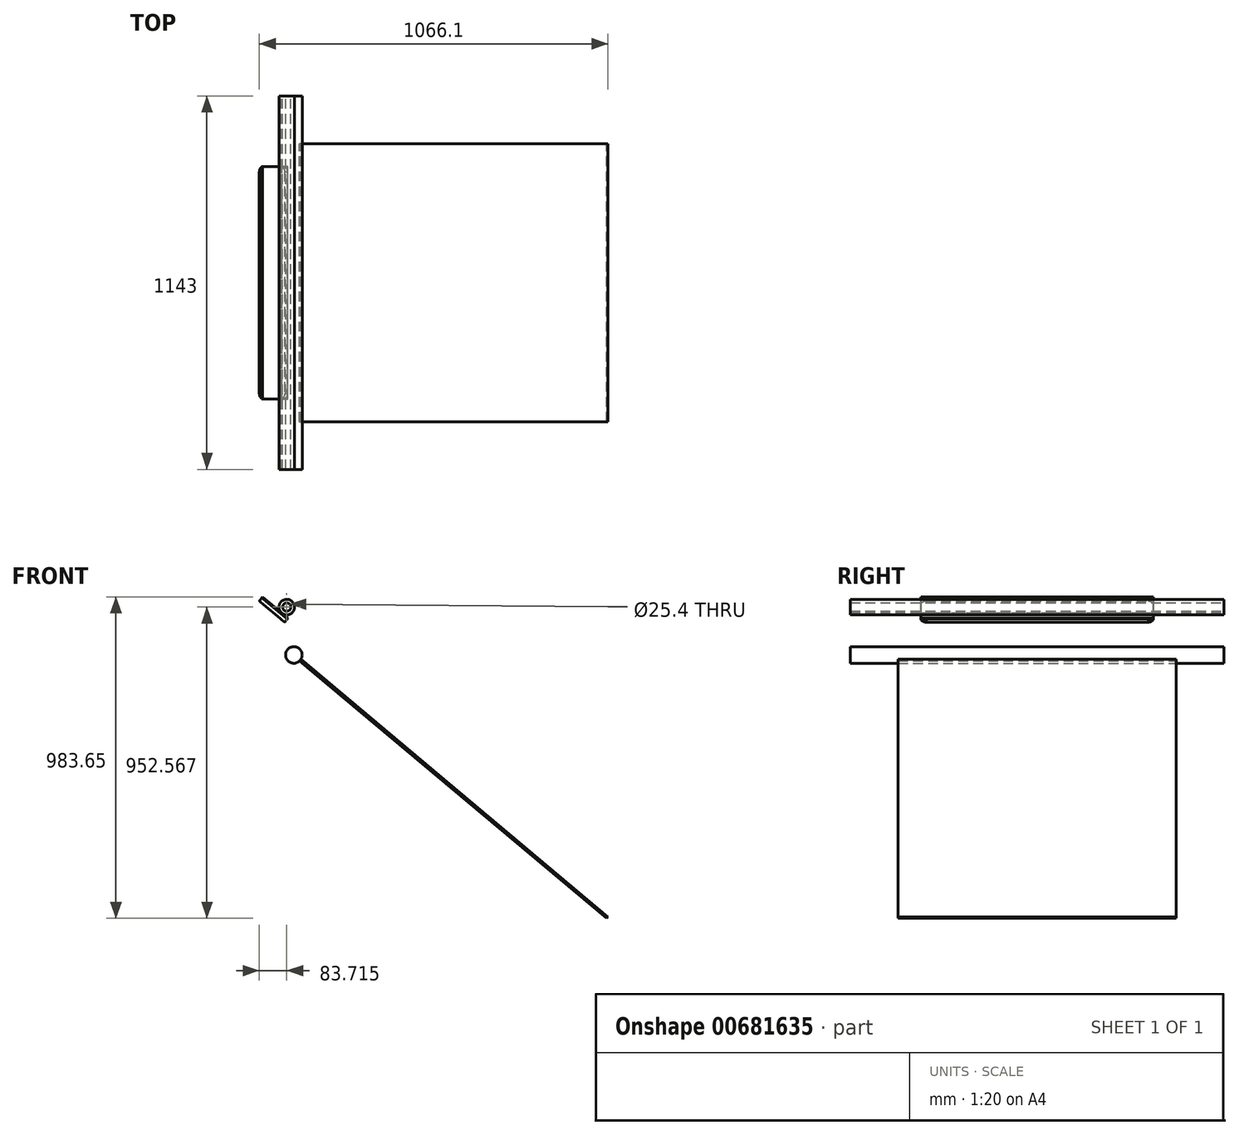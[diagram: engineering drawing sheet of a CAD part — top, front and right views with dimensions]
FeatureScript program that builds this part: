
annotation { "Feature Type Name" : "Feature", "Feature Type Description" : "" }
export const myFeature = defineFeature(function(context is Context, id is Id, definition is map)
    precondition{}
    {
        {
            var Q0;
            Q0=qCreatedBy(makeId("Front.planeOp"),FACE);
            var sketch = newSketch(context, id + "F0", { "sketchPlane" : qUnion([Q0])});
            skCircle(sketch, "E0", {"center": v(-203.72, 333.8) * mm, "radius": 23.81 * mm});
            skCircle(sketch, "E1", {"center": v(-203.72, 333.8) * mm, "radius": 12.7 * mm});
            skLineSegment(sketch, "E2", {"start": v(-179.5, 190.05) * mm, "end": v(778.67, -613.9) * mm});
            skLineSegment(sketch, "E3", {"start": v(778.67, -613.9) * mm, "end": v(774.59, -618.77) * mm});
            skLineSegment(sketch, "E4", {"start": v(774.59, -618.77) * mm, "end": v(-183.6, 185.2) * mm});
            skCircle(sketch, "E5", {"center": v(-181.85, 187.24) * mm, "radius": 25.4 * mm});
            skLineSegment(sketch, "E6", {"start": v(-179.5, 190.05) * mm, "end": v(-183.6, 185.2) * mm});
            skLineSegment(sketch, "E7", {"start": v(-219.42, 315.9) * mm, "end": v(-277.8, 364.88) * mm});
            skLineSegment(sketch, "E8", {"start": v(-277.8, 364.88) * mm, "end": v(-279.84, 362.45) * mm});
            skLineSegment(sketch, "E9", {"start": v(-279.84, 362.45) * mm, "end": v(-202, 297.14) * mm});
            skLineSegment(sketch, "E10", {"start": v(-202, 297.14) * mm, "end": v(-199.97, 299.57) * mm});
            skLineSegment(sketch, "E11", {"start": v(-199.97, 299.57) * mm, "end": v(-219.42, 315.9) * mm});
            skLineSegment(sketch, "E12", {"start": v(-219.42, 315.9) * mm, "end": v(-253.35, 382.47) * mm, "construction": true});
            skSolve(sketch);
        }
        {
            var Q0;
            {var subQ0=sQuery(id+"F0.wireOp",EDGE,"E3");Q0=makeQuery(id+"F0.imprint","IMPRINT",FACE,{"disambiguationData":[TD([[makeQuery(id+"F0.imprint","IMPRINT",EDGE,{"derivedFrom":subQ0}),-1.0]])]});}
            extrude(context, id + "F1", {"entities" : qUnion([Q0]), "endBound" : BoundingType.SYMMETRIC, "depth" : 850.9 * mm, "offsetDistance" : 25.4 * mm});
        }
        {
            var Q0;
            {var subQ0=sQuery(id+"F0.wireOp",EDGE,"E6");Q0=makeQuery(id+"F0.imprint","IMPRINT",FACE,{"disambiguationData":[TD([[makeQuery(id+"F0.imprint","IMPRINT",EDGE,{"derivedFrom":subQ0}),1.0]])]});}
            var Q1;
            {var subQ0=sQuery(id+"F0.wireOp",EDGE,"E6");Q1=makeQuery(id+"F0.imprint","IMPRINT",FACE,{"disambiguationData":[TD([[makeQuery(id+"F0.imprint","IMPRINT",EDGE,{"derivedFrom":subQ0}),-1.0]])]});}
            extrude(context, id + "F2", {"entities" : qUnion([Q0, Q1]), "operationType" : NewBodyOperationType.ADD, "endBound" : BoundingType.SYMMETRIC, "depth" : 1143 * mm, "offsetDistance" : 25.4 * mm});
        }
        {
            var Q0;
            Q0=makeQuery(id+"F0.imprint","IMPRINT",FACE,{"disambiguationData":[TD([[makeQuery(id+"F0.imprint","IMPRINT",EDGE,{"derivedFrom":sQuery(id+"F0.wireOp",EDGE,"E1")}),-1.0]])]});
            extrude(context, id + "F3", {"entities" : qUnion([Q0]), "endBound" : BoundingType.SYMMETRIC, "depth" : 1143 * mm, "offsetDistance" : 25.4 * mm});
        }
        {
            var Q0;
            {var subQ0=sQuery(id+"F0.wireOp",EDGE,"E7");Q0=makeQuery(id+"F0.imprint","IMPRINT",FACE,{"disambiguationData":[TD([[makeQuery(id+"F0.imprint","IMPRINT",EDGE,{"derivedFrom":subQ0}),1.0]])]});}
            extrude(context, id + "F4", {"entities" : qUnion([Q0]), "endBound" : BoundingType.SYMMETRIC, "depth" : 711.2 * mm, "offsetDistance" : 25.4 * mm});
        }
        {
            var Q0;
            Q0=makeQuery(id+"F4.opExtrude","SWEPT_FACE",FACE,{"disambiguationData":[OSD([sQuery(id+"F0.wireOp",EDGE,"E9")])]});
            cPlane(context, id + "F5", {"entities" : qUnion([Q0]), "cplaneType" : CPlaneType.OFFSET, "offset" : 0 * mm, "width" : 152.4 * mm, "height" : 152.4 * mm});
        }
        {
            var Q0;
            Q0=qCreatedBy(id+"F5.planeOp",FACE);
            var sketch = newSketch(context, id + "F6", { "sketchPlane" : qUnion([Q0])});
            skLineSegment(sketch, "E13", {"start": v(-430.8, 355.7) * mm, "end": v(-362.62, 355.7) * mm});
            skArc(sketch, "E14", {"start": v(-430.8, 355.7) * mm, "mid": v(-442.02, 351) * mm, "end": v(-446.6, 339.74) * mm});
            skArc(sketch, "E15", {"start": v(-345.78, 339.89) * mm, "mid": v(-351.07, 351.12) * mm, "end": v(-362.62, 355.7) * mm});
            skArc(sketch, "E16.MirrorCS", {"start": v(-430.8, -355.7) * mm, "mid": v(-442.02, -351) * mm, "end": v(-446.6, -339.74) * mm});
            skLineSegment(sketch, "E17.MirrorCS", {"start": v(-430.8, -355.7) * mm, "end": v(-362.62, -355.7) * mm});
            skArc(sketch, "E18.MirrorCS", {"start": v(-345.78, -339.89) * mm, "mid": v(-351.07, -351.12) * mm, "end": v(-362.62, -355.7) * mm});
            skLineSegment(sketch, "E19", {"start": v(-446.6, 339.74) * mm, "end": v(-446.6, -339.74) * mm});
            skLineSegment(sketch, "E20", {"start": v(-345.78, -339.89) * mm, "end": v(-345.78, 339.89) * mm});
            skSolve(sketch);
        }
        {
            var Q0;
            Q0=makeQuery(id+"F6.imprint","IMPRINT",FACE,{"disambiguationData":[TD([[makeQuery(id+"F6.imprint","IMPRINT",EDGE,{"derivedFrom":sQuery(id+"F6.wireOp",EDGE,"E13")}),-1.0]])]});
            extrude(context, id + "F7", {"entities" : qUnion([Q0]), "operationType" : NewBodyOperationType.ADD, "depth" : 12.7 * mm, "offsetDistance" : 25.4 * mm});
        }
    });
